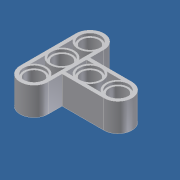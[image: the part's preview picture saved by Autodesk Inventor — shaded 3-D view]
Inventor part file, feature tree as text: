
AUTODESK INVENTOR PART (.ipt)
format: ipt  version: 2016 (Build 200138000, 138)  size: 220,672 bytes
history: native  units: mm
features: extrude x7, sketch x7
ambient origin geometry x8: Origin, YZ Plane, XZ Plane, XY Plane, X Axis, Y Axis, Z Axis, Center Point
bodies: Solid1 (feature_tree)
feature tree (14):
  extrude  "Extrusion1"  Depth=4.0mm
  extrude  "Extrusion2"  Depth=16.0mm
  extrude  "Extrusion3"  Depth=16.0mm
  extrude  "Extrusion4"  TaperAngle=0.0deg  [1 undecoded]
  extrude  "Extrusion5"  Depth=8.0mm TaperAngle=0.0deg
  extrude  "Extrusion6"  Depth=10.0mm
  extrude  "Extrusion7"  Depth=0.8mm
  sketch  "Sketch1"  dims[d3=4.0mm d4=4.0mm]
  sketch  "Sketch3"  dims[d5=4.0mm d6=16.0mm]
  sketch  "Sketch4"  dims[d8=8.0mm d10=16.0mm]
  sketch  "Sketch5"  dims[d11=0.0mm d12=0.0mm]
  sketch  "Sketch6"  dims[d13=4.0mm d14=8.0mm d15=0.0mm]
  sketch  "Sketch7"  dims[d24=5.0mm d25=10.0mm d27=10.0mm d28=20.0mm d30=8.0mm]
  sketch  "Sketch8"  dims[d32=8.0mm d33=0.0mm d34=5.0mm d35=10.0mm d37=10.0mm d38=30.0mm d40=8.0mm d42=8.0mm d43=0.0mm d44=6.0mm d45=6.0mm d46=6.0mm d47=6.0mm d48=6.0mm d49=0.8mm d50=0.0mm d52=6.0mm d53=6.0mm d54=6.0mm d55=6.0mm d56=6.0mm d57=0.8mm d58=0.0mm d59=3.5mm d60=3.5mm d61=10.0mm d63=10.0mm d64=20.0mm d66=8.0mm d68=0.8mm d69=0.0mm d70=7.0mm d72=3.5mm d73=3.5mm d74=3.5mm d75=2.197224mm d76=0.8mm d77=0.0mm]
note: 1 required parameter value undecoded (feature->parameter linkage not recoverable at this tier; creation-order binding heuristic only, values carry confidence <= 0.55)
